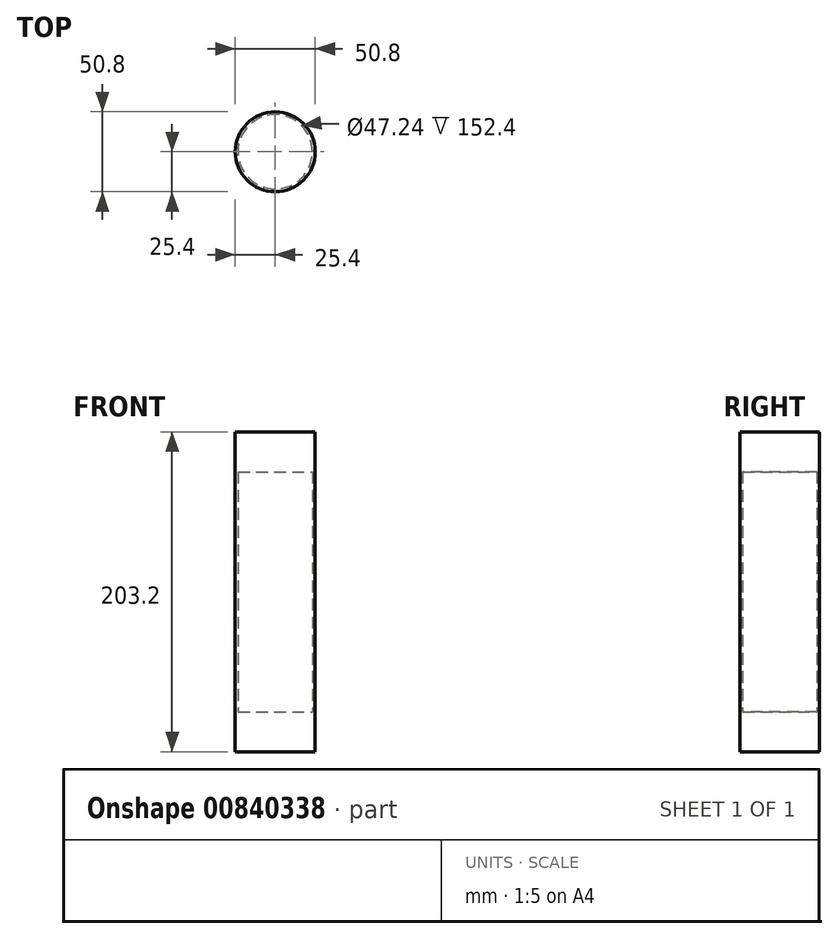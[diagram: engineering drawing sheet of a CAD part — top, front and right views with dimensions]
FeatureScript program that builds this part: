
annotation { "Feature Type Name" : "Feature", "Feature Type Description" : "" }
export const myFeature = defineFeature(function(context is Context, id is Id, definition is map)
    precondition{}
    {
        {
            var Q0;
            Q0=qCreatedBy(makeId("Front.planeOp"),FACE);
            var sketch = newSketch(context, id + "F0", { "sketchPlane" : qUnion([Q0])});
            skLineSegment(sketch, "E0.bottom", {"start": v(-25.4, 101.6) * mm, "end": v(25.4, 101.6) * mm});
            skLineSegment(sketch, "E0.top", {"start": v(-25.4, -101.6) * mm, "end": v(25.4, -101.6) * mm});
            skLineSegment(sketch, "E0.left", {"start": v(-25.4, 101.6) * mm, "end": v(-25.4, -101.6) * mm});
            skLineSegment(sketch, "E0.right", {"start": v(25.4, 101.6) * mm, "end": v(25.4, -101.6) * mm});
            skPoint(sketch, "E0.middle", {"position": v(0, 0) * mm});
            skLineSegment(sketch, "E1.bottom", {"start": v(-23.62, 76.2) * mm, "end": v(23.62, 76.2) * mm});
            skLineSegment(sketch, "E1.top", {"start": v(-23.62, -76.2) * mm, "end": v(23.62, -76.2) * mm});
            skLineSegment(sketch, "E1.left", {"start": v(-23.62, 76.2) * mm, "end": v(-23.62, -76.2) * mm});
            skLineSegment(sketch, "E1.right", {"start": v(23.62, 76.2) * mm, "end": v(23.62, -76.2) * mm});
            skLineSegment(sketch, "E2", {"start": v(0, -101.6) * mm, "end": v(0, 101.6) * mm});
            skSolve(sketch);
        }
        {
            var Q0;
            {var subQ4=sQuery(id+"F0.wireOp",EDGE,"E0.left");Q0=makeQuery(id+"F0.imprint","IMPRINT",FACE,{"disambiguationData":[TD([[makeQuery(id+"F0.imprint","IMPRINT",EDGE,{"derivedFrom":subQ4}),1.0]])]});}
            var Q1;
            Q1=sQuery(id+"F0.wireOp",EDGE,"E2");
            revolve(context, id + "F1", {"surfaceOperationType" : NewSurfaceOperationType.NEW, "entities" : qUnion([Q0]), "axis" : qUnion([Q1]), "revolveType" : RevolveType.FULL});
        }
    });
